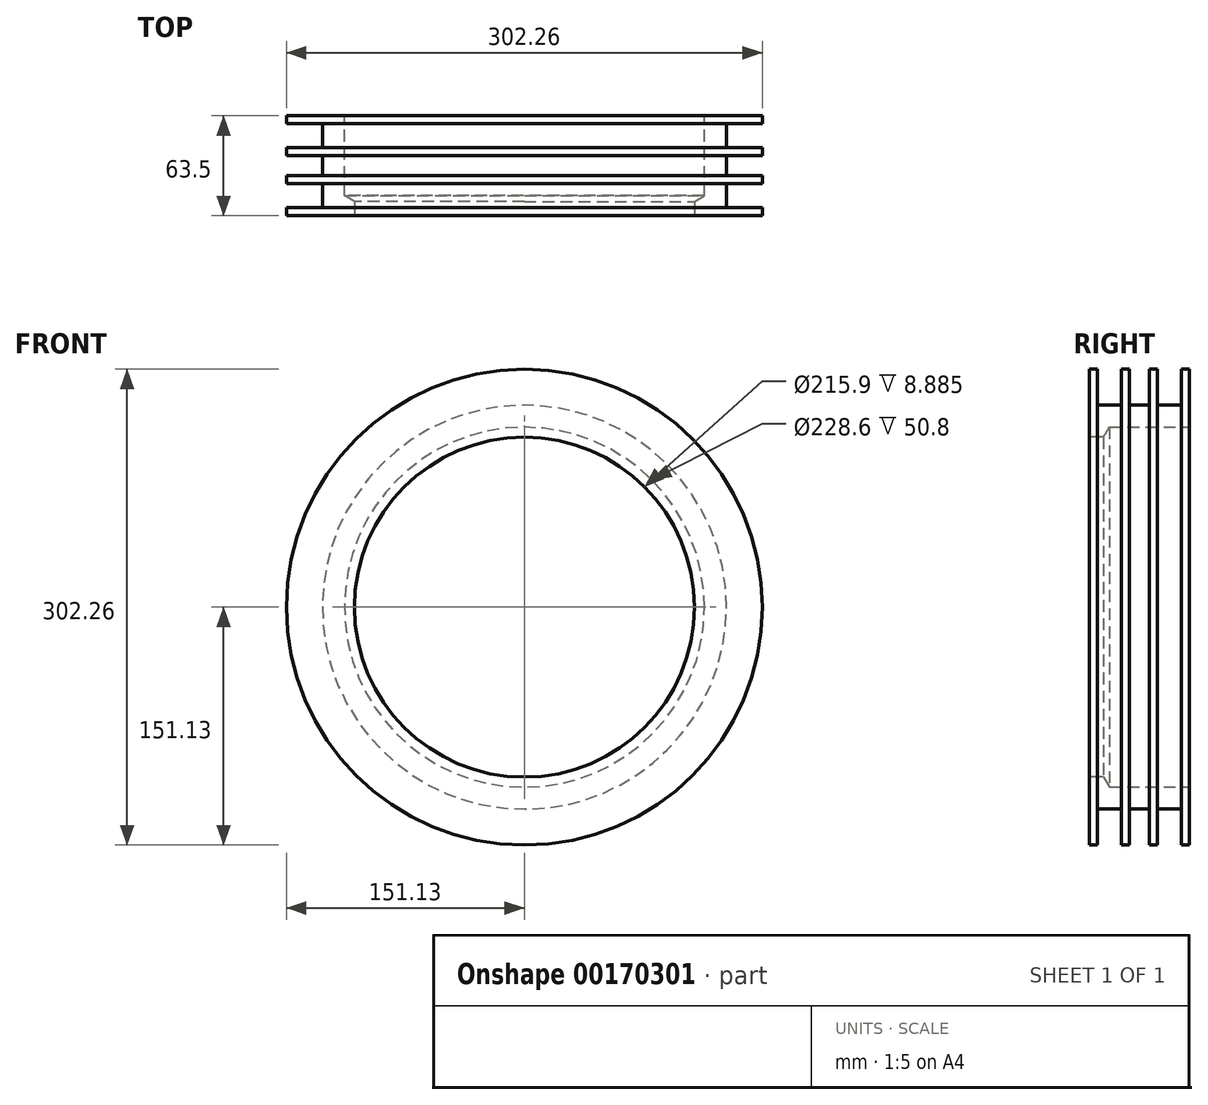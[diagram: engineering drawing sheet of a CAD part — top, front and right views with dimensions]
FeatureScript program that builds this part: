
annotation { "Feature Type Name" : "Feature", "Feature Type Description" : "" }
export const myFeature = defineFeature(function(context is Context, id is Id, definition is map)
    precondition{}
    {
        {
            var Q0;
            Q0=qCreatedBy(makeId("Front.planeOp"),FACE);
            var sketch = newSketch(context, id + "F0", { "sketchPlane" : qUnion([Q0])});
            skCircle(sketch, "E0", {"center": v(0, 0) * mm, "radius": 151.13 * mm});
            skSolve(sketch);
        }
        {
            var Q0;
            Q0=makeQuery(id+"F0.imprint","IMPRINT",FACE,{"disambiguationData":[TD([[makeQuery(id+"F0.imprint","IMPRINT",EDGE,{"derivedFrom":sQuery(id+"F0.wireOp",EDGE,"E0")}),1.0]])]});
            extrude(context, id + "F1", {"entities" : qUnion([Q0]), "depth" : 5.08 * mm});
        }
        {
            var Q0;
            Q0=makeQuery(id+"F1.opExtrude","CAP_FACE",FACE,{"disambiguationData":[OSD([sQuery(id+"F0.wireOp",EDGE,"E0")])],"isStart":false});
            var sketch = newSketch(context, id + "F2", { "sketchPlane" : qUnion([Q0])});
            skCircle(sketch, "E1", {"center": v(0, 0) * mm, "radius": 128.27 * mm});
            skSolve(sketch);
        }
        {
            var Q0;
            Q0=makeQuery(id+"F2.imprint","IMPRINT",FACE,{"disambiguationData":[TD([[makeQuery(id+"F2.imprint","IMPRINT",EDGE,{"derivedFrom":sQuery(id+"F2.wireOp",EDGE,"E1")}),1.0]])]});
            extrude(context, id + "F3", {"entities" : qUnion([Q0]), "operationType" : NewBodyOperationType.ADD, "depth" : 7.62 * mm});
        }
        {
            var Q0;
            Q0=makeQuery(id+"F3.opExtrude","CAP_FACE",FACE,{"disambiguationData":[OSD([sQuery(id+"F2.wireOp",EDGE,"E1")])],"isStart":false});
            var sketch = newSketch(context, id + "F4", { "sketchPlane" : qUnion([Q0])});
            skCircle(sketch, "E2", {"center": v(0, 0) * mm, "radius": 107.95 * mm});
            skSolve(sketch);
        }
        {
            var Q0;
            Q0=sQuery(id+"F4.wireOp",VERTEX,"E2.center");
            var Q1;
            Q1=makeQuery(id+"F1.opExtrude","SWEPT_BODY",BODY,{"disambiguationData":[OSD([sQuery(id+"F0.wireOp",EDGE,"E0")])]});
            hole(context, id + "F5", {"style" : HoleStyle.SIMPLE, "endStyle" : HoleEndStyle.THROUGH, "holeDiameter" : 215.9 * mm, "locations" : qUnion([Q0]), "scope" : qUnion([Q1]), "isTappedThrough" : true});
        }
        {
            var Q0;
            Q0=makeQuery(id+"F1.opExtrude","SWEPT_BODY",BODY,{"disambiguationData":[OSD([sQuery(id+"F0.wireOp",EDGE,"E0")])]});
            var Q1;
            Q1=makeQuery(id+"F3.opExtrude","CAP_FACE",FACE,{"disambiguationData":[OSD([sQuery(id+"F2.wireOp",EDGE,"E1")])],"isStart":false});
            mirror(context, id + "F6", {"operationType" : NewBodyOperationType.ADD, "entities" : qUnion([Q0]), "mirrorPlane" : qUnion([Q1])});
        }
        {
            var Q0;
            Q0=makeQuery(id+"F6.opPattern","COPY",FACE,{"derivedFrom":makeQuery(id+"F1.opExtrude","CAP_FACE",FACE,{"disambiguationData":[OSD([sQuery(id+"F0.wireOp",EDGE,"E0")])],"isStart":true}),"instanceName":"1"});
            var sketch = newSketch(context, id + "F7", { "sketchPlane" : qUnion([Q0])});
            skCircle(sketch, "E3", {"center": v(0, 0) * mm, "radius": 128.27 * mm});
            skSolve(sketch);
        }
        {
            var Q0;
            Q0=makeQuery(id+"F7.imprint","IMPRINT",FACE,{"disambiguationData":[TD([[makeQuery(id+"F7.imprint","IMPRINT",EDGE,{"derivedFrom":sQuery(id+"F7.wireOp",EDGE,"E3")}),1.0]])]});
            extrude(context, id + "F8", {"entities" : qUnion([Q0]), "operationType" : NewBodyOperationType.ADD, "depth" : 6.35 * mm});
        }
        {
            var Q0;
            Q0=makeQuery(id+"F1.opExtrude","SWEPT_BODY",BODY,{"disambiguationData":[OSD([sQuery(id+"F0.wireOp",EDGE,"E0")])]});
            var Q1;
            Q1=makeQuery(id+"F8.opExtrude","CAP_FACE",FACE,{"disambiguationData":[OSD([sQuery(id+"F0.wireOp",EDGE,"E0"),sQuery(id+"F5.hole-0.sketch.wireOp",EDGE,"core_line_2"),sQuery(id+"F7.wireOp",EDGE,"E3")])],"isStart":false});
            mirror(context, id + "F9", {"operationType" : NewBodyOperationType.ADD, "entities" : qUnion([Q0]), "mirrorPlane" : qUnion([Q1])});
        }
        {
            var Q0;
            Q0=makeQuery(id+"F1.opExtrude","CAP_FACE",FACE,{"disambiguationData":[OSD([sQuery(id+"F0.wireOp",EDGE,"E0")])],"isStart":true});
            var sketch = newSketch(context, id + "F10", { "sketchPlane" : qUnion([Q0])});
            skCircle(sketch, "E4", {"center": v(0, 0) * mm, "radius": 114.3 * mm});
            skSolve(sketch);
        }
        {
            var Q0;
            Q0=sQuery(id+"F10.wireOp",VERTEX,"E4.center");
            var Q1;
            Q1=makeQuery(id+"F1.opExtrude","SWEPT_BODY",BODY,{"disambiguationData":[OSD([sQuery(id+"F0.wireOp",EDGE,"E0")])]});
            hole(context, id + "F11", {"style" : HoleStyle.SIMPLE, "endStyle" : HoleEndStyle.BLIND, "holeDiameter" : 228.6 * mm, "holeDepth" : 50.8 * mm, "locations" : qUnion([Q0]), "scope" : qUnion([Q1])});
        }
    });
